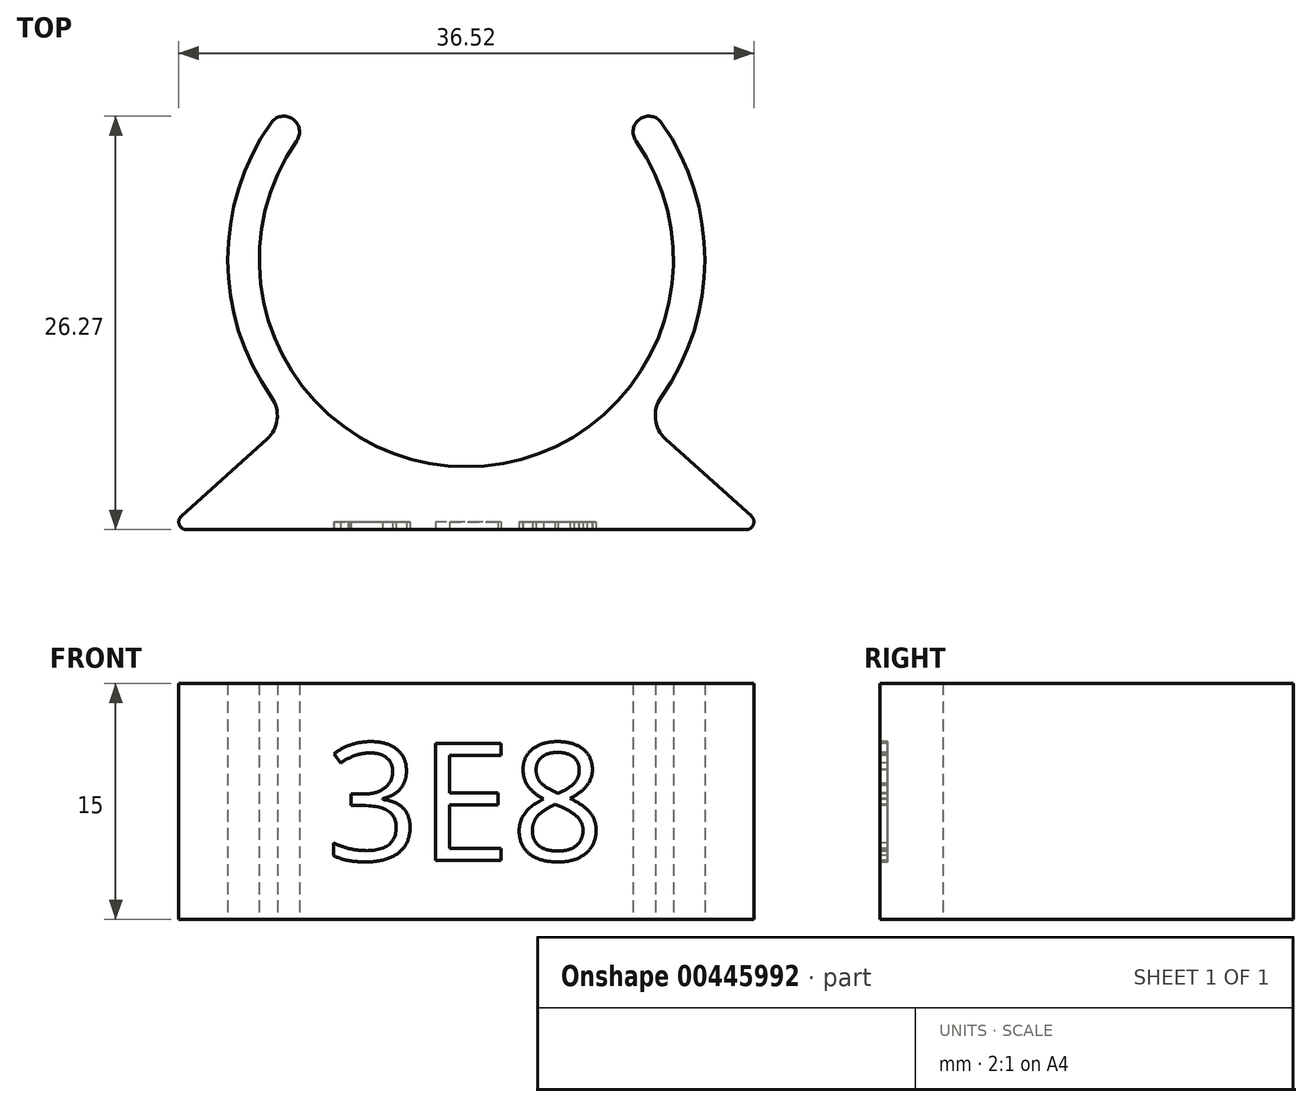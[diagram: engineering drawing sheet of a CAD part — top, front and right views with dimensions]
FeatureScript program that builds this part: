
annotation { "Feature Type Name" : "Feature", "Feature Type Description" : "" }
export const myFeature = defineFeature(function(context is Context, id is Id, definition is map)
    precondition{}
    {
        {
            assignVariable(context, id + "F0", {"name" : "WallThick", "anyValue" : 2});
        }
        {
            assignVariable(context, id + "F1", {"name" : "ExtrudeThick", "anyValue" : 15});
        }
        {
            var Q0;
            Q0=qCreatedBy(makeId("Top.planeOp"),FACE);
            var sketch = newSketch(context, id + "F2", { "sketchPlane" : qUnion([Q0])});
            skLineSegment(sketch, "E0", {"start": v(13.15, 0) * mm, "end": v(-13.15, 0) * mm, "construction": true});
            skArc(sketch, "E1", {"start": v(-10.77, 7.54) * mm, "mid": v(0, -13.15) * mm, "end": v(10.77, 7.54) * mm});
            skLineSegment(sketch, "E2", {"start": v(10.77, 7.54) * mm, "end": v(-10.77, 7.54) * mm, "construction": true});
            skLineSegment(sketch, "E3", {"start": v(0, 0) * mm, "end": v(0, 7.54) * mm, "construction": true});
            skArc(sketch, "E4.0", {"start": v(-12.41, 8.69) * mm, "mid": v(0, -15.15) * mm, "end": v(12.41, 8.69) * mm});
            skArc(sketch, "E5", {"start": v(12.41, 8.69) * mm, "mid": v(11.02, 8.94) * mm, "end": v(10.77, 7.54) * mm});
            skLineSegment(sketch, "E6", {"start": v(0, 0) * mm, "end": v(-12.41, 8.69) * mm, "construction": true});
            skArc(sketch, "E7", {"start": v(-10.77, 7.54) * mm, "mid": v(-11.02, 8.94) * mm, "end": v(-12.41, 8.69) * mm});
            skLineSegment(sketch, "E8.MirrorCS", {"start": v(0, 0) * mm, "end": v(12.41, 8.69) * mm, "construction": true});
            skLineSegment(sketch, "E9", {"start": v(0, 0) * mm, "end": v(-19.07, -17.15) * mm, "construction": true});
            skPoint(sketch, "E9.endSnap0", {"position": v(0, -17.15) * mm});
            skLineSegment(sketch, "E10", {"start": v(-19.07, -17.15) * mm, "end": v(-11.26, -10.13) * mm});
            skLineSegment(sketch, "E11", {"start": v(-19.07, -17.15) * mm, "end": v(19.07, -17.15) * mm});
            skLineSegment(sketch, "E12", {"start": v(0, -15.15) * mm, "end": v(0, -17.15) * mm, "construction": true});
            skLineSegment(sketch, "E13.MirrorCS", {"start": v(19.07, -17.15) * mm, "end": v(11.26, -10.13) * mm});
            skSolve(sketch);
        }
        {
            var Q0;
            Q0 = qSketchRegion(id + "F2", true);
            extrude(context, id + "F3", {"entities" : qUnion([Q0]), "depth" : (getVariable(context, 'ExtrudeThick')) * mm});
        }
        {
            var Q0;
            Q0=makeQuery(id+"F3.opExtrude","SWEPT_EDGE",EDGE,{"disambiguationData":[OSD([sQuery(id+"F2.wireOp",EDGE,"E4.0"),sQuery(id+"F2.wireOp",EDGE,"Q4sHdCxM-siue-C81l-TW2R-xAQugkQNyLJU")])]});
            var Q1;
            Q1=makeQuery(id+"F3.opExtrude","SWEPT_EDGE",EDGE,{"disambiguationData":[OSD([sQuery(id+"F2.wireOp",EDGE,"E4.0"),sQuery(id+"F2.wireOp",EDGE,"E10")])]});
            fillet(context, id + "F4", {"entities" : qUnion([Q0, Q1]), "radius" : (getVariable(context, 'WallThick')) * mm, "tangentPropagation" : true, "allowEdgeOverflow" : false});
        }
        {
            var Q0;
            Q0=makeQuery(id+"F3.opExtrude","SWEPT_EDGE",EDGE,{"disambiguationData":[OSD([sQuery(id+"F2.wireOp",EDGE,"E10"),sQuery(id+"F2.wireOp",EDGE,"E11")])]});
            var Q1;
            Q1=makeQuery(id+"F3.opExtrude","SWEPT_EDGE",EDGE,{"disambiguationData":[OSD([sQuery(id+"F2.wireOp",EDGE,"E11"),sQuery(id+"F2.wireOp",EDGE,"Q4sHdCxM-siue-C81l-TW2R-xAQugkQNyLJU")])]});
            fillet(context, id + "F5", {"entities" : qUnion([Q0, Q1]), "radius" : .5 * mm, "tangentPropagation" : true, "allowEdgeOverflow" : false});
        }
        {
            var Q0;
            Q0=makeQuery(id+"F3.opExtrude","SWEPT_FACE",FACE,{"disambiguationData":[OSD([sQuery(id+"F2.wireOp",EDGE,"E11")])]});
            var sketch = newSketch(context, id + "F6", { "sketchPlane" : qUnion([Q0])});
            skPoint(sketch, "E14.0", {"position": v(-10.77, 15) * mm});
            skPoint(sketch, "E15.0", {"position": v(10.77, 15) * mm});
            skPoint(sketch, "E16.0", {"position": v(-10.77, 0) * mm});
            skPoint(sketch, "E17.0", {"position": v(10.77, 0) * mm});
            skText(sketch, "E18", { "text": "3E8", "fontName": "OpenSans-Regular.ttf"});
            skLineSegment(sketch, "E19", {"start": v(-10.77, 15) * mm, "end": v(10.77, 0) * mm, "construction": true});
            skPoint(sketch, "E20", {"position": v(0, 7.5) * mm});
            const initialGuessF6  = {"E18": [-0.00892, 0.00375, 1, 0, 0.0075]};
            skSetInitialGuess(sketch, initialGuessF6);
            skSolve(sketch);
        }
        {
            var Q0;
            Q0 = qSketchRegion(id + "F6", true);
            extrude(context, id + "F7", {"entities" : qUnion([Q0]), "operationType" : NewBodyOperationType.REMOVE, "oppositeDirection" : true, "depth" : .5 * mm});
        }
    });
